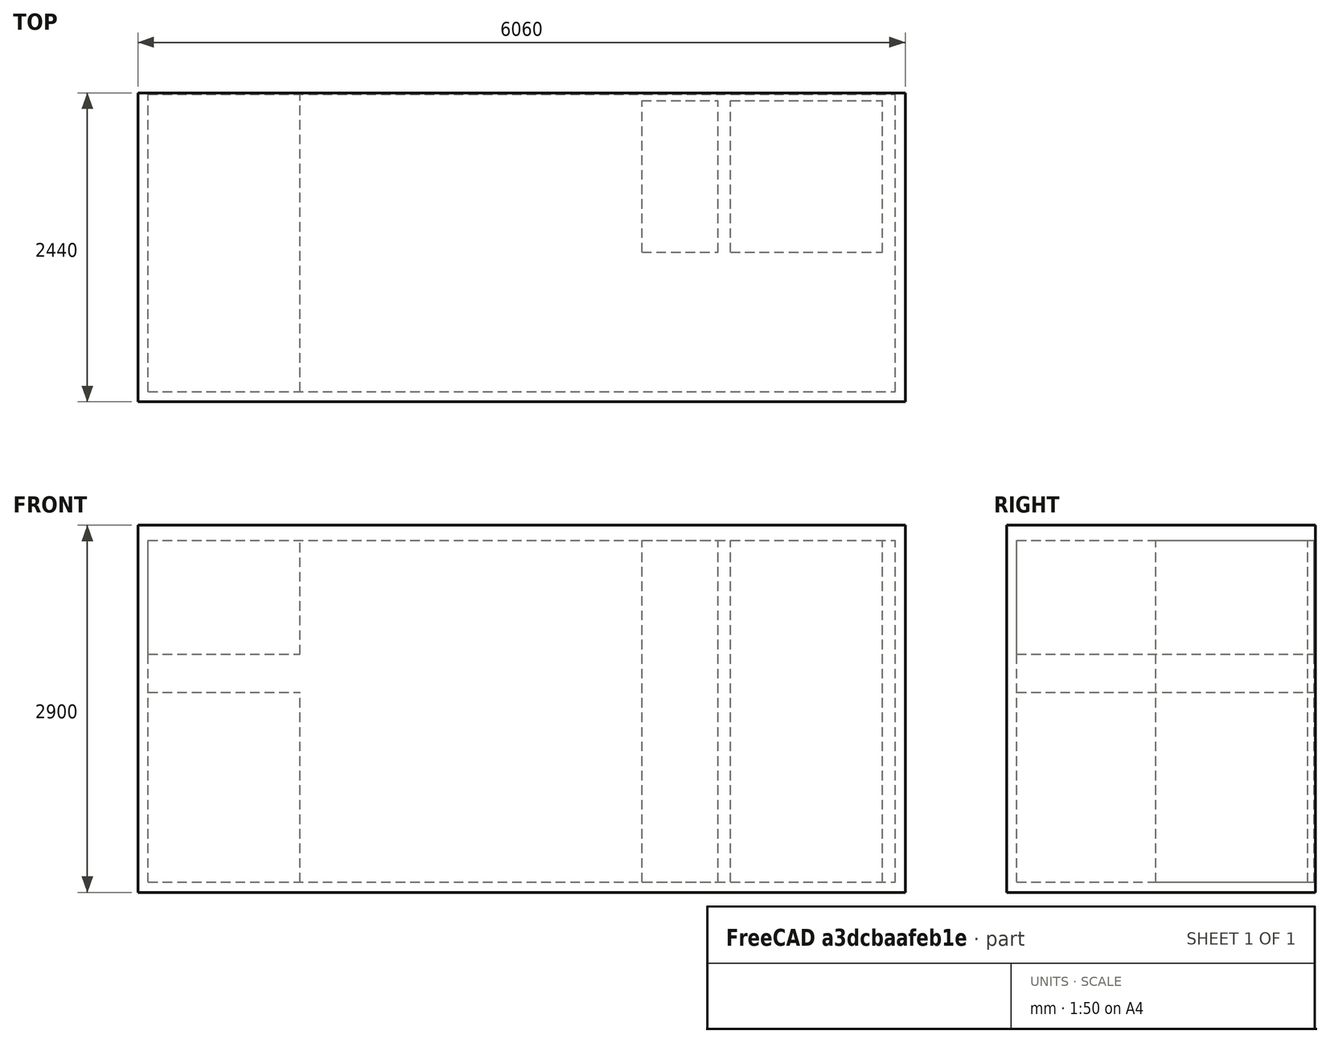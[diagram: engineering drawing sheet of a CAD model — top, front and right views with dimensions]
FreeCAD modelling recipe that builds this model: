
FCSTD DOCUMENT  (FreeCAD 0.16RUnknown)
Label: microhouse-container
License: All rights reserved
LicenseURL: http://en.wikipedia.org/wiki/All_rights_reserved
objects: Part::Box×6, Sketcher::SketchObject×1
note: 7 computed .brp shape members not serialized (recipe doc carries the construction recipe); baked Part::Feature solids carry a one-line shape summary decoded from their .brp

FEATURE [Part::Box] Box  label="ref-20'hc-outer"
  Height = 2900
  Length = 6060
  Placement = pos=(-80,-80,-80) rot=(0,0,1;0rad)
  Width = 2440
FEATURE [Part::Box] Box001  label="ref-20'fc-inner"
  Height = 2700
  Length = 5900
  Width = 2350
FEATURE [Part::Box] Box002  label="bed"
  Height = 900
  Length = 1200
  Placement = pos=(0,0,1800) rot=(0,0,1;0rad)
  Width = 2350
FEATURE [Part::Box] Box003  label="desk"
  Height = 1500
  Length = 1200
  Width = 2350
FEATURE [Part::Box] Box004  label="kichenette"
  Height = 2700
  Length = 600
  Placement = pos=(3900,1100,0) rot=(0,0,1;0rad)
  Width = 1200
FEATURE [Part::Box] Box005  label="bathroom"
  Height = 2700
  Length = 1200
  Placement = pos=(4600,1100,0) rot=(0,0,1;0rad)
  Width = 1200
FEATURE [Sketcher::SketchObject] Sketch
  sketch-geometry (4):
    g0: LineSegment StartX=1868.37 StartY=2263.48 StartZ=0 EndX=3868.37 EndY=2263.48 EndZ=0
    g1: LineSegment StartX=3868.37 StartY=2263.48 StartZ=0 EndX=3868.37 EndY=1063.48 EndZ=0
    g2: LineSegment StartX=3868.37 StartY=1063.48 StartZ=0 EndX=1868.37 EndY=1063.48 EndZ=0
    g3: LineSegment StartX=1868.37 StartY=1063.48 StartZ=0 EndX=1868.37 EndY=2263.48 EndZ=0
  constraints (10):
    c: Coincident(g0,g1)
    c: Coincident(g1,g2)
    c: Coincident(g2,g3)
    c: Coincident(g3,g0)
    c: Horizontal(g0)
    c: Horizontal(g2)
    c: Vertical(g1)
    c: Vertical(g3)
    c: DistanceX(g2,g2) = 2000
    c: DistanceY(g3,g3) = 1200
